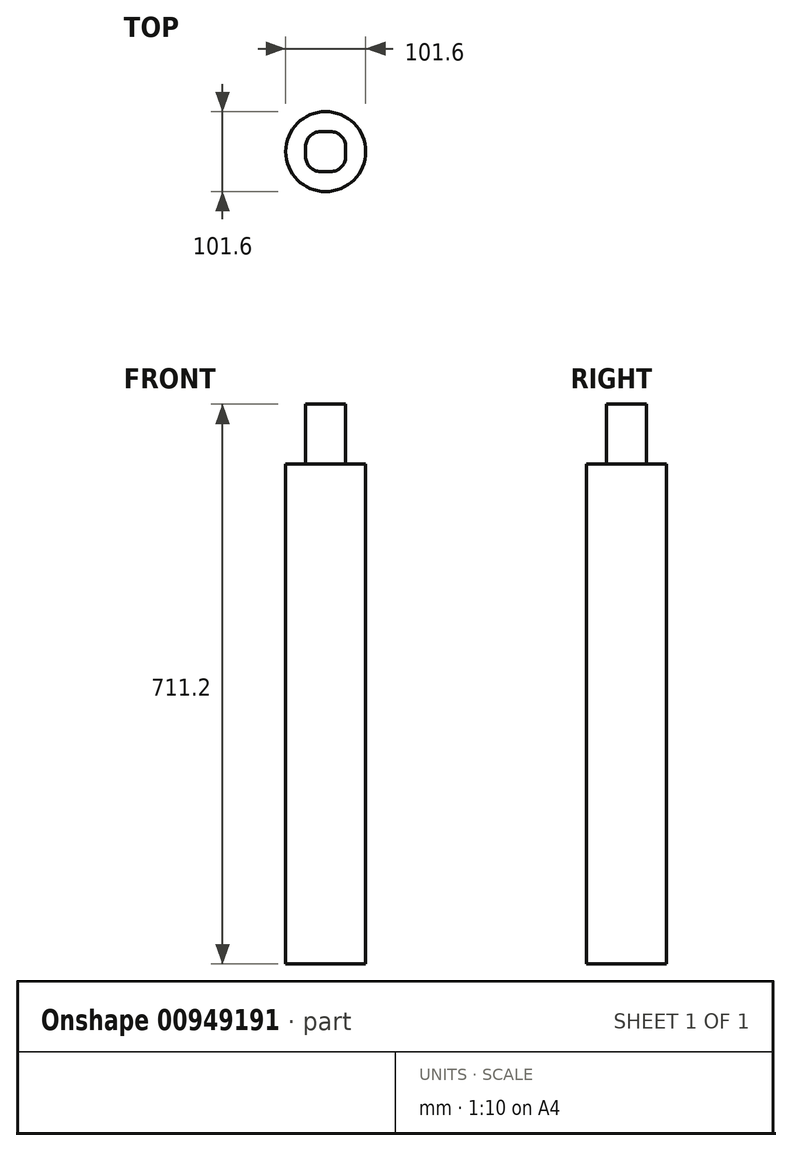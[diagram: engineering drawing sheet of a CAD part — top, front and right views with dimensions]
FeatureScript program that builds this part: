
annotation { "Feature Type Name" : "Feature", "Feature Type Description" : "" }
export const myFeature = defineFeature(function(context is Context, id is Id, definition is map)
    precondition{}
    {
        {
            var Q0;
            Q0=qCreatedBy(makeId("Top.planeOp"),FACE);
            var sketch = newSketch(context, id + "F0", { "sketchPlane" : qUnion([Q0])});
            skCircle(sketch, "E0", {"center": v(0, 0) * mm, "radius": 50.8 * mm});
            skSolve(sketch);
        }
        {
            var Q0;
            Q0=makeQuery(id+"F0.imprint","IMPRINT",FACE,{"disambiguationData":[TD([[makeQuery(id+"F0.imprint","IMPRINT",EDGE,{"derivedFrom":sQuery(id+"F0.wireOp",EDGE,"E0")}),1.0]])]});
            extrude(context, id + "F1", {"entities" : qUnion([Q0]), "depth" : 635 * mm, "offsetDistance" : 25.4 * mm});
        }
        {
            var Q0;
            Q0=makeQuery(id+"F1.opExtrude","CAP_FACE",FACE,{"disambiguationData":[OSD([sQuery(id+"F0.wireOp",EDGE,"E0")])],"isStart":false});
            var sketch = newSketch(context, id + "F2", { "sketchPlane" : qUnion([Q0])});
            skLineSegment(sketch, "E1.bottom", {"start": v(-25.4, 25.4) * mm, "end": v(25.4, 25.4) * mm});
            skLineSegment(sketch, "E1.top", {"start": v(-25.4, -25.4) * mm, "end": v(25.4, -25.4) * mm});
            skLineSegment(sketch, "E1.left", {"start": v(-25.4, 25.4) * mm, "end": v(-25.4, -25.4) * mm});
            skLineSegment(sketch, "E1.right", {"start": v(25.4, 25.4) * mm, "end": v(25.4, -25.4) * mm});
            skPoint(sketch, "E1.middle", {"position": v(0, 0) * mm});
            skSolve(sketch);
        }
        {
            var Q0;
            Q0=makeQuery(id+"F2.imprint","IMPRINT",FACE,{"disambiguationData":[TD([[makeQuery(id+"F2.imprint","IMPRINT",EDGE,{"derivedFrom":sQuery(id+"F2.wireOp",EDGE,"E1.bottom")}),-1.0]])]});
            extrude(context, id + "F3", {"entities" : qUnion([Q0]), "operationType" : NewBodyOperationType.ADD, "depth" : 76.2 * mm, "offsetDistance" : 25.4 * mm});
        }
        {
            var Q0;
            Q0=makeQuery(id+"F3.opExtrude","SWEPT_EDGE",EDGE,{"disambiguationData":[OSD([sQuery(id+"F2.wireOp",EDGE,"E1.top"),sQuery(id+"F2.wireOp",EDGE,"E1.right")])]});
            var Q1;
            Q1=makeQuery(id+"F3.opExtrude","SWEPT_EDGE",EDGE,{"disambiguationData":[OSD([sQuery(id+"F2.wireOp",EDGE,"E1.top"),sQuery(id+"F2.wireOp",EDGE,"E1.left")])]});
            var Q2;
            Q2=makeQuery(id+"F3.opExtrude","SWEPT_EDGE",EDGE,{"disambiguationData":[OSD([sQuery(id+"F2.wireOp",EDGE,"E1.bottom"),sQuery(id+"F2.wireOp",EDGE,"E1.right")])]});
            var Q3;
            Q3=makeQuery(id+"F3.opExtrude","SWEPT_EDGE",EDGE,{"disambiguationData":[OSD([sQuery(id+"F2.wireOp",EDGE,"E1.bottom"),sQuery(id+"F2.wireOp",EDGE,"E1.left")])]});
            fillet(context, id + "F4", {"entities" : qUnion([Q0, Q1, Q2, Q3]), "tangentPropagation" : true, "radius" : 19.05 * mm, "defaultsChanged" : true, "vertexSettings" : [], "allowEdgeOverflow" : false});
        }
    });
